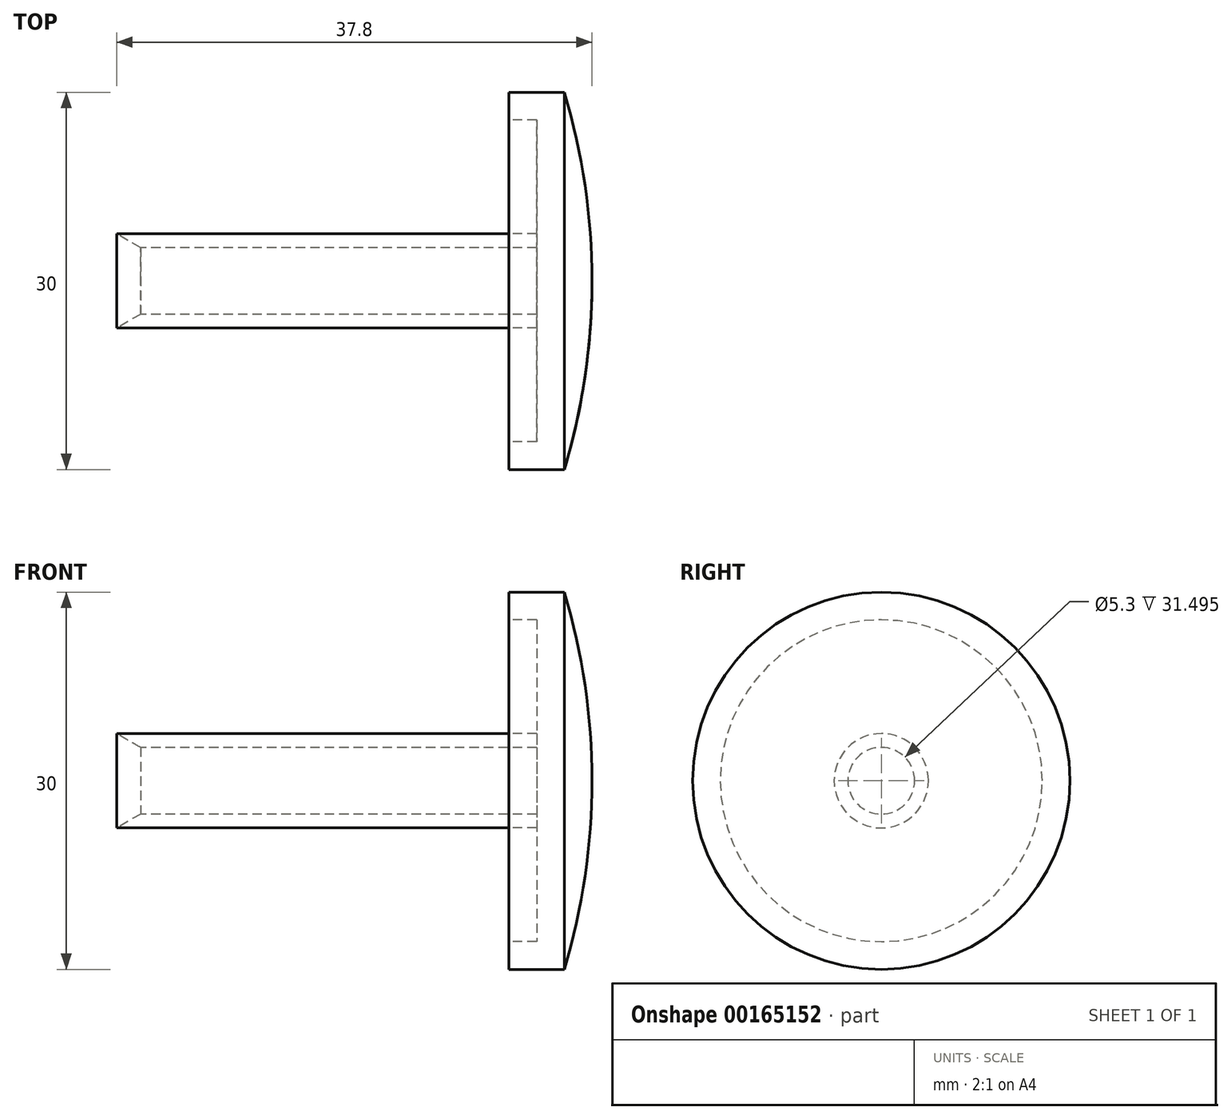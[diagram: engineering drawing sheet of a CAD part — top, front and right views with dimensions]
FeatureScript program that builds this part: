
annotation { "Feature Type Name" : "Feature", "Feature Type Description" : "" }
export const myFeature = defineFeature(function(context is Context, id is Id, definition is map)
    precondition{}
    {
        {
            var Q0;
            Q0=qCreatedBy(makeId("Top.planeOp"),FACE);
            var sketch = newSketch(context, id + "F0", { "sketchPlane" : qUnion([Q0])});
            skLineSegment(sketch, "E0", {"start": v(0, 0) * mm, "end": v(33.4, 0) * mm, "construction": true});
            skLineSegment(sketch, "E1", {"start": v(33.4, 0) * mm, "end": v(33.4, 2.65) * mm});
            skLineSegment(sketch, "E2", {"start": v(1.9, 2.65) * mm, "end": v(33.4, 2.65) * mm});
            skLineSegment(sketch, "E3", {"start": v(0, 3.75) * mm, "end": v(33.4, 3.75) * mm});
            skLineSegment(sketch, "E4", {"start": v(0, 3.75) * mm, "end": v(1.9, 2.65) * mm});
            skPoint(sketch, "E5.end.orphan", {"position": v(0, 2.65) * mm});
            skLineSegment(sketch, "E6", {"start": v(33.4, 15) * mm, "end": v(35.6, 15) * mm});
            skPoint(sketch, "E7.center.orphan", {"position": v(-14.44, 0) * mm});
            skArc(sketch, "E8", {"start": v(37.8, 0) * mm, "mid": v(37.25, 7.58) * mm, "end": v(35.6, 15) * mm});
            skPoint(sketch, "E9.start.orphan", {"position": v(35.6, 0) * mm});
            skLineSegment(sketch, "E10", {"start": v(33.4, 0) * mm, "end": v(37.8, 0) * mm});
            skPoint(sketch, "E10.endSnap0", {"position": v(37.8, 0) * mm});
            skPoint(sketch, "E11.orphan", {"position": v(35.6, -15) * mm});
            skPoint(sketch, "E12.orphan", {"position": v(45.16, 0) * mm});
            skLineSegment(sketch, "E13.trimOffspring", {"start": v(33.4, 3.75) * mm, "end": v(33.4, 12.8) * mm});
            skLineSegment(sketch, "E14", {"start": v(33.4, 15) * mm, "end": v(31.2, 15) * mm});
            skLineSegment(sketch, "E15", {"start": v(31.2, 15) * mm, "end": v(31.2, 12.8) * mm});
            skLineSegment(sketch, "E16", {"start": v(31.2, 12.8) * mm, "end": v(33.4, 12.8) * mm});
            skSolve(sketch);
        }
        {
            var Q0;
            Q0 = qSketchRegion(id + "F0", true);
            var Q1;
            Q1=sQuery(id+"F0.wireOp",EDGE,"E0");
            revolve(context, id + "F1", {"entities" : qUnion([Q0]), "axis" : qUnion([Q1]), "revolveType" : RevolveType.FULL});
        }
    });
